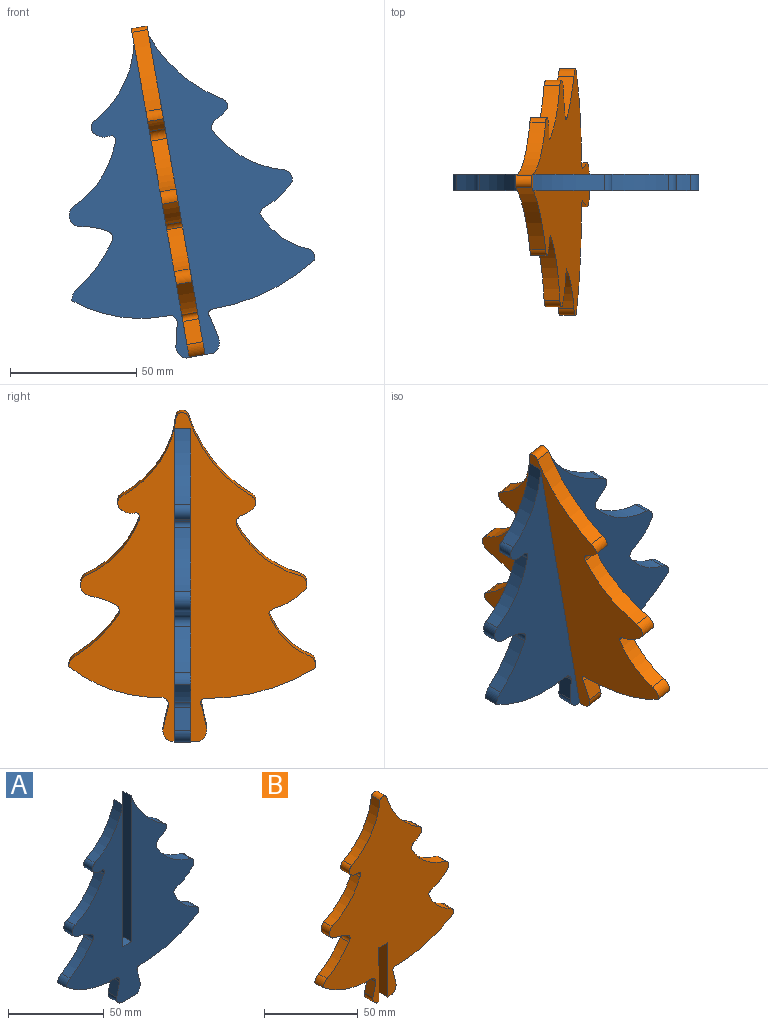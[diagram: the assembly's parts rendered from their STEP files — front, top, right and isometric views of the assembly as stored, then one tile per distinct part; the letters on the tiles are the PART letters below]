
ASSEMBLY  parts=2 mates=1
PART A: 34 faces, bbox 97.9x6.4x128.6 mm
  f0: plane 11.17x6.35mm, normal (0.01,0,-1), area 70.9mm2, adj f1,f31,f32,f33
  f1: cylinder r=5.39mm len=6.35mm, axis (0,1,0), area 39.5mm2, adj f0,f2,f32,f33
  f2: plane 9.26x6.35mm, normal (0.98,0,0.22), area 60.2mm2, adj f1,f3,f32,f33
  f3: cylinder r=1.77mm len=6.35mm, axis (0,1,0), area 25.1mm2, adj f2,f4,f32,f33
  f4: cylinder r=80.88mm len=43.4mm, axis (0,1,0), area 289.9mm2, adj f3,f5,f32,f33
  f5: cylinder r=3.81mm len=6.35mm, axis (0,1,0), area 41.6mm2, adj f4,f6,f32,f33
  f6: cylinder r=28.98mm len=16.86mm, axis (0,1,0), area 150mm2, adj f5,f7,f32,f33
  f7: cylinder r=3.65mm len=6.35mm, axis (0,1,0), area 19.7mm2, adj f6,f8,f32,f33
  f8: cylinder r=25.31mm len=12.73mm, axis (0,1,0), area 97.2mm2, adj f7,f9,f32,f33
  f9: cylinder r=3.94mm len=6.35mm, axis (0,1,0), area 38.7mm2, adj f8,f10,f32,f33
  f10: cylinder r=40.51mm len=25.41mm, axis (0,1,0), area 212.9mm2, adj f9,f11,f32,f33
  f11: cylinder r=3.5mm len=6.35mm, axis (0,1,0), area 30.2mm2, adj f10,f12,f32,f33
  f12: cylinder r=12.17mm len=6.35mm, axis (0,1,0), area 44.6mm2, adj f11,f13,f32,f33
  f13: cylinder r=3.56mm len=6.35mm, axis (0,1,0), area 31.7mm2, adj f12,f14,f32,f33
  f14: cylinder r=57.1mm len=29.45mm, axis (0,1,0), area 245mm2, adj f13,f15,f32,f33
  f15: plane 93.22x6.35mm, normal (-1,0,0), area 591.9mm2, adj f14,f16,f32,f33
  f16: plane 6.35x6.35mm, normal (0,0,1), area 40.3mm2, adj f15,f17,f32,f33
  f17: plane 90.86x6.35mm, normal (1,0,0), area 576.9mm2, adj f16,f18,f32,f33
  f18: cylinder r=41.38mm len=27.09mm, axis (0,1,0), area 221.9mm2, adj f17,f19,f32,f33
  f19: cylinder r=3.33mm len=6.35mm, axis (0,1,0), area 50mm2, adj f18,f20,f32,f33
  f20: cylinder r=5.94mm len=6.35mm, axis (0,1,0), area 34.2mm2, adj f19,f21,f32,f33
  f21: cylinder r=2.02mm len=6.35mm, axis (0,1,0), area 27mm2, adj f20,f22,f32,f33
  f22: cylinder r=39.07mm len=22.01mm, axis (0,1,0), area 198.3mm2, adj f21,f23,f32,f33
  f23: cylinder r=4.48mm len=8.1mm, axis (0,1,0), area 66.5mm2, adj f22,f24,f32,f33
  f24: cylinder r=29.07mm len=10.24mm, axis (0,1,0), area 69.1mm2, adj f23,f25,f32,f33
  f25: cylinder r=3.05mm len=6.35mm, axis (0,1,0), area 37mm2, adj f24,f26,f32,f33
  f26: cylinder r=56.44mm len=16.32mm, axis (0,1,0), area 144.6mm2, adj f25,f27,f32,f33
  f27: cylinder r=5.44mm len=6.35mm, axis (0,1,0), area 35.2mm2, adj f26,f28,f32,f33
  f28: cylinder r=56.73mm len=37.47mm, axis (0,1,0), area 256.2mm2, adj f27,f29,f32,f33
  f29: cylinder r=3.22mm len=6.35mm, axis (0,1,0), area 29mm2, adj f28,f30,f32,f33
  f30: plane 8.9x6.35mm, normal (-0.97,0,0.23), area 58.1mm2, adj f29,f31,f32,f33
  f31: cylinder r=4.54mm len=6.35mm, axis (0,1,0), area 43.2mm2, adj f0,f30,f32,f33
  f32: plane 128.57x97.91mm, normal (0,-1,0), area 5811mm2, adj f0,f1,f2,f3,f4,f5,f6,f7
  f33: plane 128.57x97.91mm, normal (0,1,0), area 5811mm2, adj f0,f1,f2,f3,f4,f5,f6,f7
PART B: 36 faces, bbox 97.9x6.4x132.4 mm
  f0: plane 6.35x3.67mm, normal (0.01,0,-1), area 23.3mm2, adj f1,f33,f34,f35
  f1: cylinder r=5.39mm len=6.35mm, axis (0,1,0), area 39.5mm2, adj f0,f2,f34,f35
  f2: plane 9.26x6.35mm, normal (0.98,0,0.22), area 60.2mm2, adj f1,f3,f34,f35
  f3: cylinder r=1.77mm len=6.35mm, axis (0,1,0), area 25.1mm2, adj f2,f4,f34,f35
  f4: cylinder r=80.88mm len=43.4mm, axis (0,1,0), area 289.9mm2, adj f3,f5,f34,f35
  f5: cylinder r=3.81mm len=6.35mm, axis (0,1,0), area 41.6mm2, adj f4,f6,f34,f35
  f6: cylinder r=28.98mm len=16.86mm, axis (0,1,0), area 150mm2, adj f5,f7,f34,f35
  f7: cylinder r=3.65mm len=6.35mm, axis (0,1,0), area 19.7mm2, adj f6,f8,f34,f35
  f8: cylinder r=25.31mm len=12.73mm, axis (0,1,0), area 97.2mm2, adj f7,f9,f34,f35
  f9: cylinder r=3.94mm len=6.35mm, axis (0,1,0), area 38.7mm2, adj f8,f10,f34,f35
  f10: cylinder r=40.51mm len=25.41mm, axis (0,1,0), area 212.9mm2, adj f9,f11,f34,f35
  f11: cylinder r=3.5mm len=6.35mm, axis (0,1,0), area 30.2mm2, adj f10,f12,f34,f35
  f12: cylinder r=12.17mm len=6.35mm, axis (0,1,0), area 44.6mm2, adj f11,f13,f34,f35
  f13: cylinder r=3.56mm len=6.35mm, axis (0,1,0), area 31.7mm2, adj f12,f14,f34,f35
  f14: cylinder r=57.1mm len=31.85mm, axis (0,1,0), area 261mm2, adj f13,f15,f34,f35
  f15: cylinder r=2.69mm len=6.35mm, axis (0,1,0), area 37.1mm2, adj f14,f16,f34,f35
  f16: cylinder r=41.38mm len=31.85mm, axis (0,1,0), area 252.6mm2, adj f15,f17,f34,f35
  f17: cylinder r=3.33mm len=6.35mm, axis (0,1,0), area 50mm2, adj f16,f18,f34,f35
  f18: cylinder r=5.94mm len=6.35mm, axis (0,1,0), area 34.2mm2, adj f17,f19,f34,f35
  f19: cylinder r=2.02mm len=6.35mm, axis (0,1,0), area 27mm2, adj f18,f20,f34,f35
  f20: cylinder r=39.07mm len=22.01mm, axis (0,1,0), area 198.3mm2, adj f19,f21,f34,f35
  f21: cylinder r=4.48mm len=8.1mm, axis (0,1,0), area 66.5mm2, adj f20,f22,f34,f35
  f22: cylinder r=29.07mm len=10.24mm, axis (0,1,0), area 69.1mm2, adj f21,f23,f34,f35
  f23: cylinder r=3.05mm len=6.35mm, axis (0,1,0), area 37mm2, adj f22,f24,f34,f35
  f24: cylinder r=56.44mm len=16.32mm, axis (0,1,0), area 144.6mm2, adj f23,f25,f34,f35
  f25: cylinder r=5.44mm len=6.35mm, axis (0,1,0), area 35.2mm2, adj f24,f26,f34,f35
  f26: cylinder r=56.73mm len=37.47mm, axis (0,1,0), area 256.2mm2, adj f25,f27,f34,f35
  f27: cylinder r=3.22mm len=6.35mm, axis (0,1,0), area 29mm2, adj f26,f28,f34,f35
  f28: plane 8.9x6.35mm, normal (-0.97,0,0.23), area 58.1mm2, adj f27,f29,f34,f35
  f29: cylinder r=4.54mm len=6.35mm, axis (0,1,0), area 43.2mm2, adj f28,f30,f34,f35
  f30: plane 6.35x1.15mm, normal (0.01,0,-1), area 7.3mm2, adj f29,f31,f34,f35
  f31: plane 35.34x6.35mm, normal (1,0,0), area 224.4mm2, adj f30,f32,f34,f35
  f32: plane 6.35x6.35mm, normal (0,0,-1), area 40.3mm2, adj f31,f33,f34,f35
  f33: plane 35.3x6.35mm, normal (-1,0,0), area 224.1mm2, adj f0,f32,f34,f35
  f34: plane 132.41x97.91mm, normal (0,-1,0), area 6195.7mm2, adj f0,f1,f2,f3,f4,f5,f6,f7
  f35: plane 132.41x97.91mm, normal (0,1,0), area 6195.7mm2, adj f0,f1,f2,f3,f4,f5,f6,f7
PLACE A rot(axis=(0,-1,0),10deg) t=(-36.17,-14.59,-0.63)mm
PLACE B rot(axis=(0.09,-0.09,-0.99),90.4deg) t=(-32.43,-17.06,0.04)mm
MATE planar B.f34 <-> A.f17  axis (-0.98,0,-0.17) through (-34.13,-21.07,-26.88)mm
